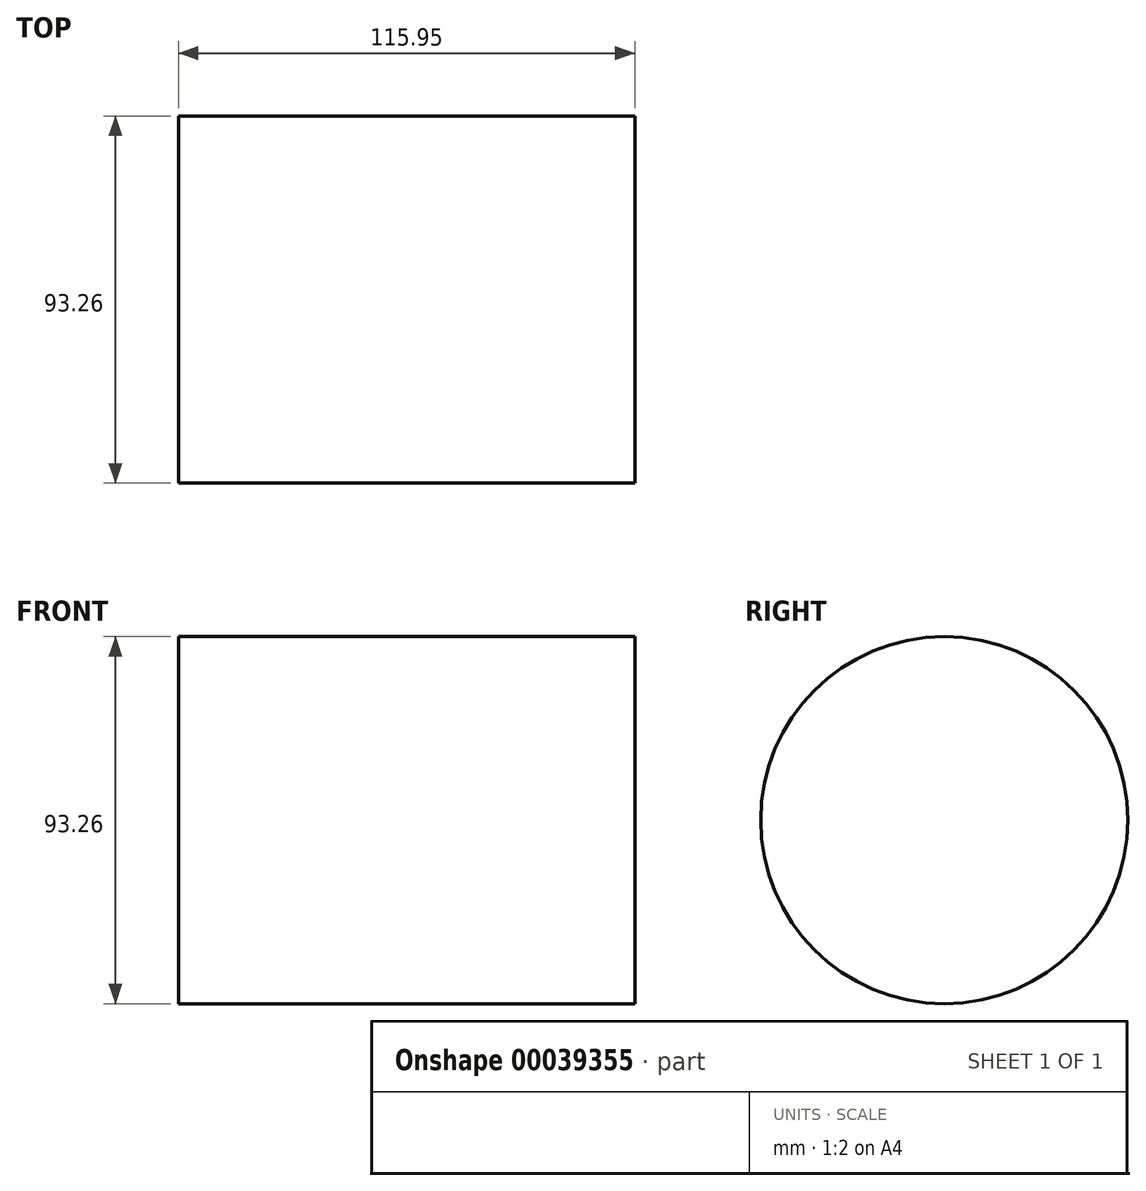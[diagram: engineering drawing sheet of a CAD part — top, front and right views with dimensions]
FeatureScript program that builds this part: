
annotation { "Feature Type Name" : "Feature", "Feature Type Description" : "" }
export const myFeature = defineFeature(function(context is Context, id is Id, definition is map)
    precondition{}
    {
        {
            var Q0;
            Q0=qCreatedBy(makeId("Right.planeOp"),FACE);
            var sketch = newSketch(context, id + "F0", { "sketchPlane" : qUnion([Q0])});
            skCircle(sketch, "E0", {"center": v(0, 0) * mm, "radius": 46.63 * mm});
            skSolve(sketch);
        }
        {
            var Q0;
            Q0 = qSketchRegion(id + "F0", true);
            extrude(context, id + "F1", {"entities" : qUnion([Q0]), "oppositeDirection" : true, "depth" : 52.6 * mm, "hasSecondDirection" : true, "secondDirectionOppositeDirection" : false, "secondDirectionDepth" : 63.36 * mm});
        }
    });
